# Revit family: led-e-gu10-7_5w-4000k-36d-dim_140060955_fdba
name_source: partatom
category: Leuchten
revit_build: Autodesk Revit 2016 (Build: 20190508_0715(x64)
units: mm (PartAtom-declared; Revit-internal decimal feet)

## family parameters
Basisbauteil = Fläche
Beim Laden mit Abzugskörper schneiden = Nein
Bemaßung runder Anschluss = Durchmesser verwenden
Gemeinsam genutzt = Nein
Lichtquelle = Nein
Raumberechnungspunkt = Nein
Teiletyp = Normal

## types (1)
- LED-E-GU10-7,5W-4000K-36D-DIM (1 x LED, 575 lm)
    Approval mark = CE
    Beschreibung = Full retrofit of existing halogen GU10 lamps. Light silver coloured. No UV/IR radiation. Significantly lower heat output than halogen, avoiding discolouration and risk of damaging goods. Up to 87% lower energy consumption than halogen.
    CIE Flux Codes = 88 96 99 99 101
    Height = 57 mm
    Hersteller = OPPLE
    Lamp Light Flux = 575 lm
    Lamp count = 1
    Lampe = 1 x LED
    Length = 50 mm
    Luminous efficacy = 73 lm/W
    ModVariant = Nein
    Modell = 140060955
    Mounting Place = Ceiling
    Mounting Type = Surface mounted
    Number of Poles = 1
    OnlyDefault = Ja
    Power Factor = 1
    Product Name = LED-E-GU10-7,5W-4000K-36D-DIM
    Product group = Reflector EcoMax GU10
    ProductGroupID = 325
    Protection Class = Protection class I
    Protection Degree = IP 20
    RLX_Detail_Level = 1
    RlxData = <blob elided: 31029 chars, md5=793604de>
    Scheinlast = 8 VA
    Socket = socket
    Standby Power = 0 W
    System Light Flux = 578 lm
    System Power = 8 W
    Typenbild = 140060955.jpg
    Typenkommentare = Product without accessories
    URL = http://relux.com
    VarID = ---
    Voltage = 0 V
    Vorgabe-Ansicht = 1800 mm
    Weight = 0.00 kg
    Width = 0 mm  [stored 0 ft]

note: [stored X ft] marks values corroborated as IEEE doubles in the binary element streams (Revit-internal decimal feet)

## geometry (parser evidence)
native form markers: Blend x4, Sweep x10
no freeform markers — native parametric forms only
